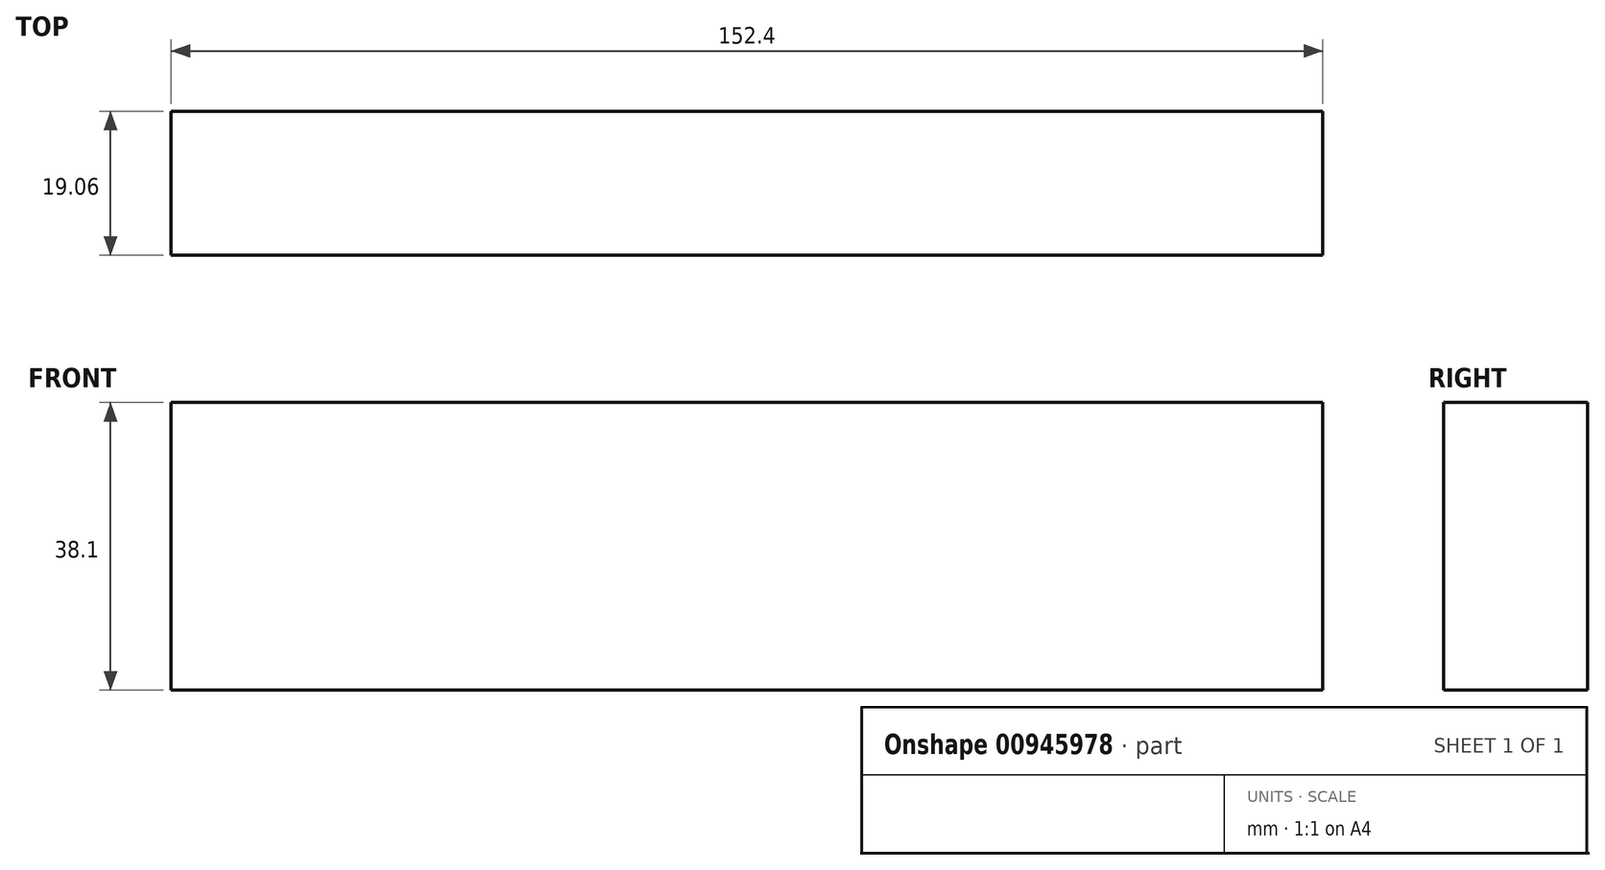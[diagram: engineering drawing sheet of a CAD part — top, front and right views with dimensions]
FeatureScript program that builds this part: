
annotation { "Feature Type Name" : "Feature", "Feature Type Description" : "" }
export const myFeature = defineFeature(function(context is Context, id is Id, definition is map)
    precondition{}
    {
        {
            var Q0;
            Q0=qCreatedBy(makeId("Top.planeOp"), FACE);
            var sketch = newSketch(context, id + "F0", { "sketchPlane" : qUnion([Q0])});
            skLineSegment(sketch, "E0.bottom", {"start": v(76.2, -9.52) * mm, "end": v(-76.2, -9.53) * mm});
            skLineSegment(sketch, "E0.top", {"start": v(76.2, 9.53) * mm, "end": v(-76.2, 9.52) * mm});
            skLineSegment(sketch, "E0.left", {"start": v(76.2, -9.52) * mm, "end": v(76.2, 9.53) * mm});
            skLineSegment(sketch, "E0.right", {"start": v(-76.2, -9.53) * mm, "end": v(-76.2, 9.52) * mm});
            skPoint(sketch, "E0.middle", {"position": v(0, 0) * mm});
            skSolve(sketch);
        }
        {
            var Q0;
            Q0 = qSketchRegion(id + "F0", true);
            extrude(context, id + "F1", {"entities" : qUnion([Q0]), "oppositeDirection" : true, "depth" : 38.1 * mm, "offsetDistance" : 25.4 * mm});
        }
    });
